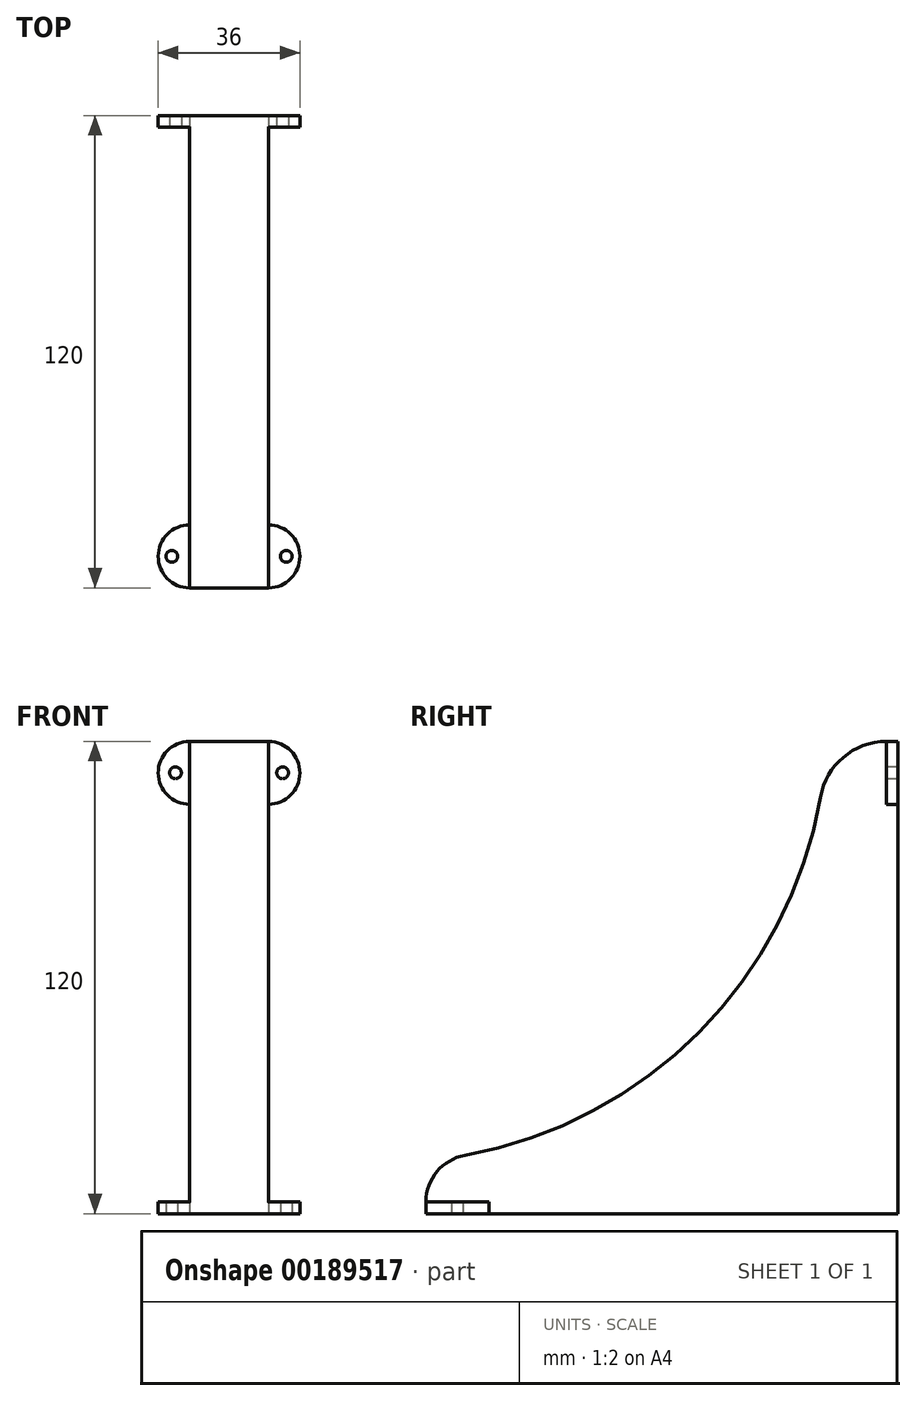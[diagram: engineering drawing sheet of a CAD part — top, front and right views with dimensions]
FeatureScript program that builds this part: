
annotation { "Feature Type Name" : "Feature", "Feature Type Description" : "" }
export const myFeature = defineFeature(function(context is Context, id is Id, definition is map)
    precondition{}
    {
        {
            var Q0;
            Q0=qCreatedBy(makeId("Top.planeOp"),FACE);
            var sketch = newSketch(context, id + "F0", { "sketchPlane" : qUnion([Q0])});
            skLineSegment(sketch, "E0.bottom", {"start": v(-10, 64.96) * mm, "end": v(10, 64.96) * mm});
            skLineSegment(sketch, "E0.top", {"start": v(-10, -55.04) * mm, "end": v(10, -55.04) * mm});
            skLineSegment(sketch, "E0.left", {"start": v(-10, 64.96) * mm, "end": v(-10, -55.04) * mm});
            skLineSegment(sketch, "E0.right", {"start": v(10, 64.96) * mm, "end": v(10, -55.04) * mm});
            skPoint(sketch, "E0.middle", {"position": v(0, 4.96) * mm});
            skLineSegment(sketch, "E1", {"start": v(-8, 64.96) * mm, "end": v(-8, -55.04) * mm});
            skLineSegment(sketch, "E2", {"start": v(-10, 44.96) * mm, "end": v(-8, 44.96) * mm});
            skArc(sketch, "E3", {"start": v(-10, -39.04) * mm, "mid": v(-18, -47.04) * mm, "end": v(-10, -55.04) * mm});
            skArc(sketch, "E4", {"start": v(10, -55.04) * mm, "mid": v(18, -47.04) * mm, "end": v(10, -39.04) * mm});
            skCircle(sketch, "E5", {"center": v(-14.53, -47.04) * mm, "radius": 1.5 * mm});
            skCircle(sketch, "E6", {"center": v(14.53, -47.04) * mm, "radius": 1.5 * mm});
            skLineSegment(sketch, "E7", {"start": v(0, 0) * mm, "end": v(0, -55.04) * mm, "construction": true});
            skLineSegment(sketch, "E8.trimOffspring", {"start": v(-10, 44.96) * mm, "end": v(10, 44.96) * mm});
            skLineSegment(sketch, "E9", {"start": v(-8, 61.96) * mm, "end": v(-10, 61.96) * mm});
            skSolve(sketch);
        }
        {
            var Q0;
            {var subQ3=sQuery(id+"F0.wireOp",EDGE,"E2");var subQ6=sQuery(id+"F0.wireOp",EDGE,"E0.left");var subQ9=makeQuery(id+"F0.imprint","INTERSECT",VERTEX,{"derivedFrom":[subQ6,subQ3]});Q0=makeQuery(id+"F0.imprint","IMPRINT",FACE,{"disambiguationData":[TD([[makeQuery(id+"F0.imprint","IMPRINT",EDGE,{"disambiguationData":[TD([[subQ9,-1.0]])],"derivedFrom":subQ6}),1.0]])]});}
            var Q1;
            {var subQ3=sQuery(id+"F0.wireOp",EDGE,"E2");var subQ6=sQuery(id+"F0.wireOp",EDGE,"E0.right");var subQ9=makeQuery(id+"F0.imprint","INTERSECT",VERTEX,{"derivedFrom":[subQ6,subQ3]});Q1=makeQuery(id+"F0.imprint","IMPRINT",FACE,{"disambiguationData":[TD([[makeQuery(id+"F0.imprint","IMPRINT",EDGE,{"disambiguationData":[TD([[subQ9,-1.0]])],"derivedFrom":subQ6}),-1.0]])]});}
            extrude(context, id + "F1", {"entities" : qUnion([Q0, Q1]), "depth" : 15 * mm});
        }
        {
            var Q0;
            {var subQ0=sQuery(id+"F0.wireOp",EDGE,"E1");var subQ1=sQuery(id+"F0.wireOp",EDGE,"E0.top");var subQ2=makeQuery(id+"F0.imprint","INTERSECT",VERTEX,{"derivedFrom":[subQ1,subQ0]});Q0=makeQuery(id+"F0.imprint","IMPRINT",FACE,{"disambiguationData":[TD([[makeQuery(id+"F0.imprint","IMPRINT",EDGE,{"disambiguationData":[TD([[subQ2,-1.0]])],"derivedFrom":subQ1}),1.0]])]});}
            var Q1;
            {var subQ0=sQuery(id+"F0.wireOp",EDGE,"E3");Q1=makeQuery(id+"F0.imprint","IMPRINT",FACE,{"disambiguationData":[TD([[makeQuery(id+"F0.imprint","IMPRINT",EDGE,{"derivedFrom":subQ0}),1.0]])]});}
            var Q2;
            {var subQ0=sQuery(id+"F0.wireOp",EDGE,"E4");Q2=makeQuery(id+"F0.imprint","IMPRINT",FACE,{"disambiguationData":[TD([[makeQuery(id+"F0.imprint","IMPRINT",EDGE,{"derivedFrom":subQ0}),1.0]])]});}
            extrude(context, id + "F2", {"entities" : qUnion([Q0, Q1, Q2]), "operationType" : NewBodyOperationType.ADD, "depth" : 3 * mm});
        }
        {
            var Q0;
            {var subQ0=sQuery(id+"F0.wireOp",EDGE,"E0.right");var subQ1=sQuery(id+"F0.wireOp",EDGE,"E0.bottom");var subQ2=makeQuery(id+"F0.imprint","INTERSECT",VERTEX,{"derivedFrom":[subQ1,subQ0]});Q0=makeQuery(id+"F0.imprint","IMPRINT",FACE,{"disambiguationData":[TD([[makeQuery(id+"F0.imprint","IMPRINT",EDGE,{"disambiguationData":[TD([[subQ2,1.0]])],"derivedFrom":subQ1}),-1.0]])]});}
            var Q1;
            {var subQ0=sQuery(id+"F0.wireOp",EDGE,"E0.left");var subQ1=sQuery(id+"F0.wireOp",EDGE,"E0.bottom");var subQ2=makeQuery(id+"F0.imprint","INTERSECT",VERTEX,{"derivedFrom":[subQ1,subQ0]});Q1=makeQuery(id+"F0.imprint","IMPRINT",FACE,{"disambiguationData":[TD([[makeQuery(id+"F0.imprint","IMPRINT",EDGE,{"disambiguationData":[TD([[subQ2,-1.0]])],"derivedFrom":subQ1}),-1.0]])]});}
            extrude(context, id + "F3", {"entities" : qUnion([Q0, Q1]), "operationType" : NewBodyOperationType.ADD, "depth" : 120 * mm});
        }
        {
            var Q0;
            {var subQ5=sQuery(id+"F0.wireOp",EDGE,"E9");Q0=makeQuery(id+"F0.imprint","IMPRINT",FACE,{"disambiguationData":[TD([[makeQuery(id+"F0.imprint","IMPRINT",EDGE,{"derivedFrom":subQ5}),-1.0]])]});}
            var Q1;
            Q1=makeQuery(id+"F3.opExtrude","CAP_FACE",FACE,{"disambiguationData":[OSD([sQuery(id+"F0.wireOp",EDGE,"E0.bottom"),sQuery(id+"F0.wireOp",EDGE,"E0.right"),sQuery(id+"F0.wireOp",EDGE,"E0.left"),sQuery(id+"F0.wireOp",EDGE,"E8.trimOffspring")])],"isStart":false});
            extrude(context, id + "F4", {"entities" : qUnion([Q0]), "operationType" : NewBodyOperationType.ADD, "endBound" : BoundingType.UP_TO_SURFACE, "endBoundEntityFace" : qUnion([Q1]), "depth" : 25 * mm});
        }
        {
            var Q0;
            {var subQ0=sQuery(id+"F0.wireOp",EDGE,"E0.right");Q0=makeQuery(id+"F3.boolean.opBoolean","MERGE",FACE,{"derivedFrom":[makeQuery(id+"F1.opExtrude","SWEPT_FACE",FACE,{"disambiguationData":[OSD([subQ0])]}),makeQuery(id+"F3.opExtrude","SWEPT_FACE",FACE,{"disambiguationData":[OSD([subQ0])]})]});}
            var sketch = newSketch(context, id + "F5", { "sketchPlane" : qUnion([Q0])});
            skLineSegment(sketch, "E10.bottom", {"start": v(64.96, 120) * mm, "end": v(61.96, 120) * mm});
            skLineSegment(sketch, "E10.top", {"start": v(64.96, 104) * mm, "end": v(61.96, 104) * mm});
            skLineSegment(sketch, "E10.left", {"start": v(64.96, 120) * mm, "end": v(64.96, 104) * mm});
            skLineSegment(sketch, "E10.right", {"start": v(61.96, 120) * mm, "end": v(61.96, 104) * mm});
            skSolve(sketch);
        }
        {
            var Q0;
            Q0=makeQuery(id+"F5.imprint","IMPRINT",FACE,{"disambiguationData":[TD([[makeQuery(id+"F5.imprint","IMPRINT",EDGE,{"derivedFrom":sQuery(id+"F5.wireOp",EDGE,"E10.bottom")}),1.0]])]});
            extrude(context, id + "F6", {"entities" : qUnion([Q0]), "operationType" : NewBodyOperationType.ADD, "depth" : 17 * mm});
        }
        {
            var Q0;
            Q0=makeQuery(id+"F6.opExtrude","SWEPT_FACE",FACE,{"disambiguationData":[OSD([sQuery(id+"F5.wireOp",EDGE,"E10.right")])]});
            var sketch = newSketch(context, id + "F7", { "sketchPlane" : qUnion([Q0])});
            skArc(sketch, "E11", {"start": v(10, 104) * mm, "mid": v(18, 112) * mm, "end": v(10, 120) * mm});
            skCircle(sketch, "E12", {"center": v(13.61, 112) * mm, "radius": 1.5 * mm});
            skSolve(sketch);
        }
        {
            var Q0;
            Q0=makeQuery(id+"F7.imprint","IMPRINT",FACE,{"disambiguationData":[TD([[makeQuery(id+"F7.imprint","IMPRINT",EDGE,{"derivedFrom":sQuery(id+"F7.wireOp",EDGE,"E11")}),-1.0]])]});
            var Q1;
            {var subQ0=sQuery(id+"F0.wireOp",EDGE,"E0.bottom");Q1=makeQuery(id+"F6.boolean.opBoolean","MERGE",FACE,{"derivedFrom":[makeQuery(id+"F4.boolean.opBoolean","MERGE",FACE,{"derivedFrom":[makeQuery(id+"F3.opExtrude","SWEPT_FACE",FACE,{"disambiguationData":[OSD([subQ0]),TDD([makeQuery(id+"F0.imprint","IMPRINT",EDGE,{"disambiguationData":[TD([[makeQuery(id+"F0.imprint","INTERSECT",VERTEX,{"derivedFrom":[subQ0,sQuery(id+"F0.wireOp",EDGE,"E0.left")]}),-1.0]])],"derivedFrom":subQ0})])]}),makeQuery(id+"F3.opExtrude","SWEPT_FACE",FACE,{"disambiguationData":[OSD([subQ0]),TDD([makeQuery(id+"F0.imprint","IMPRINT",EDGE,{"disambiguationData":[TD([[makeQuery(id+"F0.imprint","INTERSECT",VERTEX,{"derivedFrom":[subQ0,sQuery(id+"F0.wireOp",EDGE,"E0.right")]}),1.0]])],"derivedFrom":subQ0})])]}),makeQuery(id+"F4.opExtrude","SWEPT_FACE",FACE,{"disambiguationData":[OSD([subQ0])]})]}),makeQuery(id+"F6.opExtrude","SWEPT_FACE",FACE,{"disambiguationData":[OSD([sQuery(id+"F5.wireOp",EDGE,"E10.left")])]})]});}
            extrude(context, id + "F8", {"entities" : qUnion([Q0]), "operationType" : NewBodyOperationType.REMOVE, "endBound" : BoundingType.UP_TO_SURFACE, "oppositeDirection" : true, "endBoundEntityFace" : qUnion([Q1]), "depth" : 25 * mm});
        }
        {
            var Q0;
            Q0=makeQuery(id+"F7.imprint","IMPRINT",FACE,{"disambiguationData":[TD([[makeQuery(id+"F7.imprint","IMPRINT",EDGE,{"derivedFrom":sQuery(id+"F7.wireOp",EDGE,"E12")}),1.0]])]});
            var Q1;
            {var subQ0=sQuery(id+"F0.wireOp",EDGE,"E0.bottom");Q1=makeQuery(id+"F6.boolean.opBoolean","MERGE",FACE,{"derivedFrom":[makeQuery(id+"F4.boolean.opBoolean","MERGE",FACE,{"derivedFrom":[makeQuery(id+"F3.opExtrude","SWEPT_FACE",FACE,{"disambiguationData":[OSD([subQ0]),TDD([makeQuery(id+"F0.imprint","IMPRINT",EDGE,{"disambiguationData":[TD([[makeQuery(id+"F0.imprint","INTERSECT",VERTEX,{"derivedFrom":[subQ0,sQuery(id+"F0.wireOp",EDGE,"E0.left")]}),-1.0]])],"derivedFrom":subQ0})])]}),makeQuery(id+"F3.opExtrude","SWEPT_FACE",FACE,{"disambiguationData":[OSD([subQ0]),TDD([makeQuery(id+"F0.imprint","IMPRINT",EDGE,{"disambiguationData":[TD([[makeQuery(id+"F0.imprint","INTERSECT",VERTEX,{"derivedFrom":[subQ0,sQuery(id+"F0.wireOp",EDGE,"E0.right")]}),1.0]])],"derivedFrom":subQ0})])]}),makeQuery(id+"F4.opExtrude","SWEPT_FACE",FACE,{"disambiguationData":[OSD([subQ0])]})]}),makeQuery(id+"F6.opExtrude","SWEPT_FACE",FACE,{"disambiguationData":[OSD([sQuery(id+"F5.wireOp",EDGE,"E10.left")])]})]});}
            extrude(context, id + "F9", {"entities" : qUnion([Q0]), "operationType" : NewBodyOperationType.REMOVE, "endBound" : BoundingType.UP_TO_SURFACE, "oppositeDirection" : true, "endBoundEntityFace" : qUnion([Q1]), "depth" : 25 * mm});
        }
        {
            var Q0;
            Q0=makeQuery(id+"F3.opExtrude","CAP_VERTEX",VERTEX,{"disambiguationData":[OSD([sQuery(id+"F0.wireOp",EDGE,"E0.bottom"),sQuery(id+"F0.wireOp",EDGE,"E0.left")])],"isStart":false});
            var Q1;
            Q1=makeQuery(id+"F8.boolean.opBoolean","COPY",VERTEX,{"derivedFrom":makeQuery(id+"F8.opExtrude","CAP_VERTEX",VERTEX,{"disambiguationData":[OSD([sQuery(id+"F0.wireOp",EDGE,"E0.bottom"),sQuery(id+"F0.wireOp",EDGE,"E0.right"),sQuery(id+"F5.wireOp",EDGE,"E10.bottom"),sQuery(id+"F5.wireOp",EDGE,"E10.left"),sQuery(id+"F5.wireOp",EDGE,"E10.right"),sQuery(id+"F7.wireOp",EDGE,"E11")])],"isStart":false})});
            cPlane(context, id + "F10", {"entities" : qUnion([Q0, Q1]), "cplaneType" : CPlaneType.MID_PLANE, "offset" : 25 * mm, "width" : 150 * mm, "height" : 150 * mm});
        }
        {
            var Q0;
            Q0=makeQuery(id+"F1.opExtrude","SWEPT_BODY",BODY,{"disambiguationData":[OSD([sQuery(id+"F0.wireOp",EDGE,"E0.top"),sQuery(id+"F0.wireOp",EDGE,"E0.left"),sQuery(id+"F0.wireOp",EDGE,"E1"),sQuery(id+"F0.wireOp",EDGE,"E2")])]});
            var Q1;
            Q1=qCreatedBy(id+"F10.planeOp",FACE);
            mirror(context, id + "F11", {"operationType" : NewBodyOperationType.ADD, "entities" : qUnion([Q0]), "mirrorPlane" : qUnion([Q1])});
        }
        {
            var Q0;
            Q0=makeQuery(id+"F3.opExtrude","CAP_EDGE",EDGE,{"disambiguationData":[OSD([sQuery(id+"F0.wireOp",EDGE,"E8.trimOffspring")])],"isStart":false});
            var Q1;
            Q1=makeQuery(id+"F3.opExtrude","CAP_EDGE",EDGE,{"disambiguationData":[OSD([sQuery(id+"F0.wireOp",EDGE,"E2")])],"isStart":false});
            fillet(context, id + "F12", {"entities" : qUnion([Q0, Q1]), "radius" : 17.14 * mm, "tangentPropagation" : true, "allowEdgeOverflow" : false});
        }
        {
            var Q0;
            {var subQ0=sQuery(id+"F0.wireOp",EDGE,"E0.top");Q0=makeQuery(id+"F1.opExtrude","CAP_EDGE",EDGE,{"disambiguationData":[OSD([subQ0]),TDD([makeQuery(id+"F0.imprint","IMPRINT",EDGE,{"disambiguationData":[TD([[makeQuery(id+"F0.imprint","INTERSECT",VERTEX,{"derivedFrom":[subQ0,sQuery(id+"F0.wireOp",EDGE,"E0.left")]}),-1.0]])],"derivedFrom":subQ0})])],"isStart":false});}
            var Q1;
            {var subQ0=sQuery(id+"F0.wireOp",EDGE,"E0.top");Q1=makeQuery(id+"F1.opExtrude","CAP_EDGE",EDGE,{"disambiguationData":[OSD([subQ0]),TDD([makeQuery(id+"F0.imprint","IMPRINT",EDGE,{"disambiguationData":[TD([[makeQuery(id+"F0.imprint","INTERSECT",VERTEX,{"derivedFrom":[subQ0,sQuery(id+"F0.wireOp",EDGE,"E1")]}),1.0]])],"derivedFrom":subQ0})])],"isStart":false});}
            fillet(context, id + "F13", {"entities" : qUnion([Q0, Q1]), "radius" : 12.07 * mm, "tangentPropagation" : true, "allowEdgeOverflow" : false});
        }
        {
            var Q0;
            Q0=makeQuery(id+"F1.opExtrude","CAP_EDGE",EDGE,{"disambiguationData":[OSD([sQuery(id+"F0.wireOp",EDGE,"E8.trimOffspring")])],"isStart":false});
            var Q1;
            Q1=makeQuery(id+"F1.opExtrude","CAP_EDGE",EDGE,{"disambiguationData":[OSD([sQuery(id+"F0.wireOp",EDGE,"E2")])],"isStart":false});
            fillet(context, id + "F14", {"entities" : qUnion([Q0, Q1]), "radius" : 112.02 * mm, "tangentPropagation" : true, "allowEdgeOverflow" : false});
        }
    });
